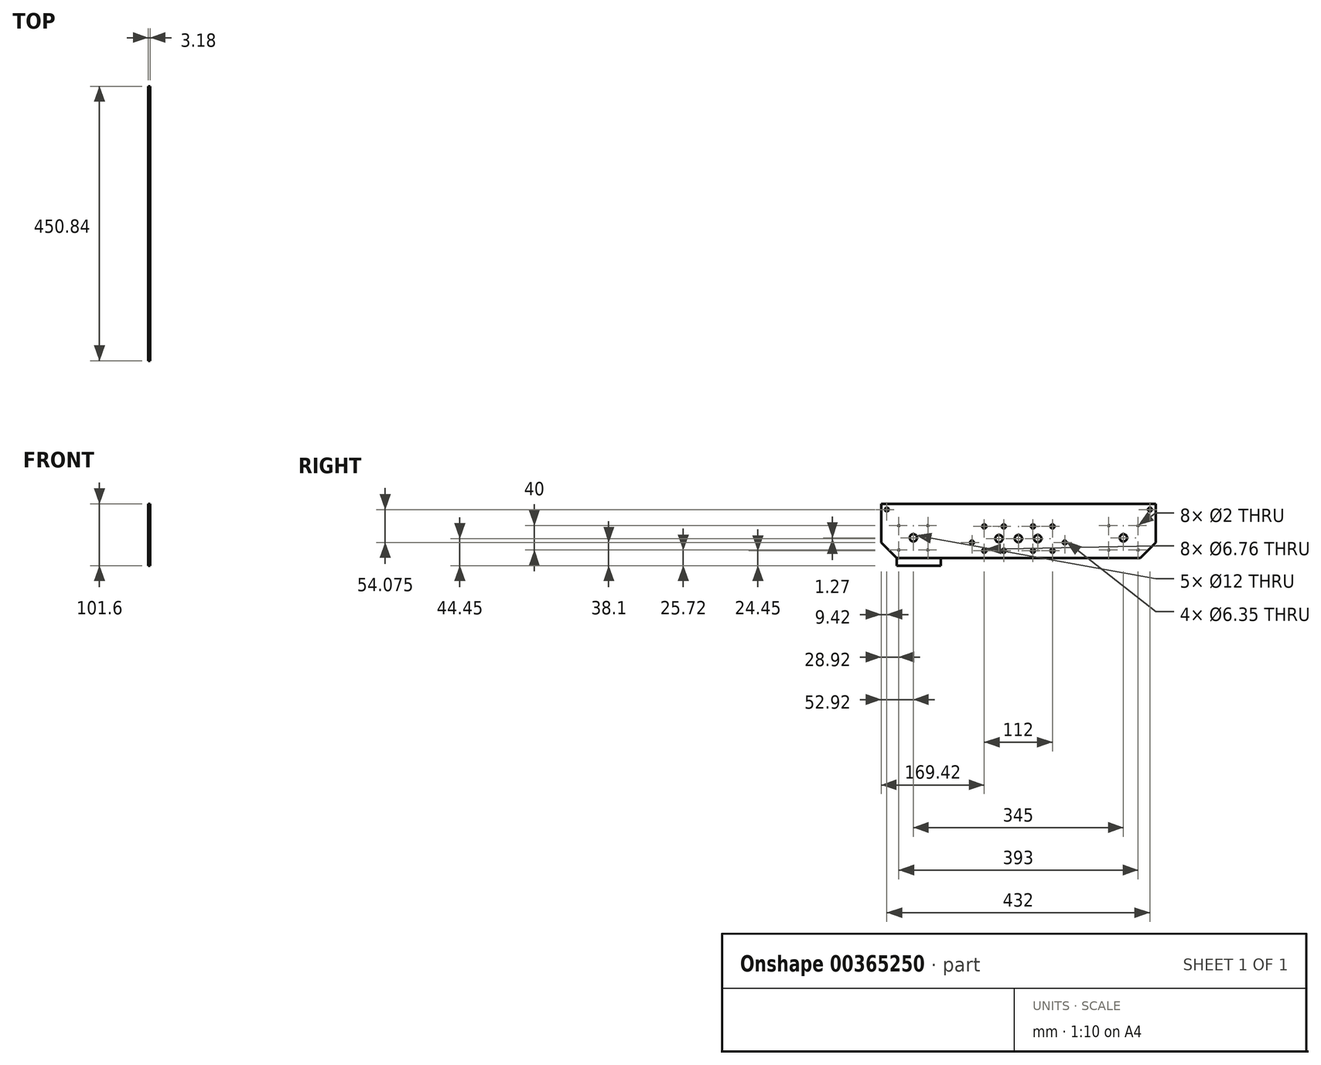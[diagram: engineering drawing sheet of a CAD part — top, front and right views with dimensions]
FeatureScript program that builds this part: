
annotation { "Feature Type Name" : "Feature", "Feature Type Description" : "" }
export const myFeature = defineFeature(function(context is Context, id is Id, definition is map)
    precondition{}
    {
        {
            var Q0;
            Q0=qCreatedBy(makeId("Right.planeOp"),FACE);
            cPlane(context, id + "F0", {"entities" : qUnion([Q0]), "cplaneType" : CPlaneType.OFFSET, "offset" : 142.88 * mm, "width" : 152.4 * mm, "height" : 152.4 * mm});
        }
        {
            var Q0;
            Q0=qCreatedBy(id+"F0.planeOp",FACE);
            var sketch = newSketch(context, id + "F1", { "sketchPlane" : qUnion([Q0])});
            skLineSegment(sketch, "E0.bottom", {"start": v(225.42, 44.45) * mm, "end": v(-225.43, 44.45) * mm});
            skLineSegment(sketch, "E0.top", {"start": v(200.02, -44.45) * mm, "end": v(-200.02, -44.45) * mm});
            skLineSegment(sketch, "E0.left", {"start": v(225.42, 44.45) * mm, "end": v(225.42, -19.05) * mm});
            skLineSegment(sketch, "E0.right", {"start": v(-225.43, 44.45) * mm, "end": v(-225.43, -19.05) * mm});
            skPoint(sketch, "E0.middle", {"position": v(0, 0) * mm});
            skLineSegment(sketch, "E1", {"start": v(-225.42, -19.05) * mm, "end": v(-200.02, -44.45) * mm});
            skLineSegment(sketch, "E2.MirrorCS", {"start": v(225.42, -19.05) * mm, "end": v(200.02, -44.45) * mm});
            skPoint(sketch, "E3.orphan", {"position": v(-225.42, -44.45) * mm});
            skLineSegment(sketch, "E4", {"start": v(-225.42, -19.05) * mm, "end": v(-225.42, -44.45) * mm, "construction": true});
            skLineSegment(sketch, "E5", {"start": v(-200.02, -44.45) * mm, "end": v(-225.42, -44.45) * mm, "construction": true});
            skPoint(sketch, "E6.orphan", {"position": v(225.43, -44.45) * mm});
            skSolve(sketch);
        }
        {
            var Q0;
            Q0=makeQuery(id+"F1.imprint","IMPRINT",FACE,{"disambiguationData":[TD([[makeQuery(id+"F1.imprint","IMPRINT",EDGE,{"derivedFrom":sQuery(id+"F1.wireOp",EDGE,"E0.bottom")}),1.0]])]});
            extrude(context, id + "F2", {"entities" : qUnion([Q0]), "depth" : 3.17 * mm, "offsetDistance" : 25.4 * mm});
        }
        {
            var Q0;
            Q0=makeQuery(id+"F2.opExtrude","CAP_FACE",FACE,{"disambiguationData":[OSD([sQuery(id+"F1.wireOp",EDGE,"E0.bottom"),sQuery(id+"F1.wireOp",EDGE,"E0.top"),sQuery(id+"F1.wireOp",EDGE,"E0.left"),sQuery(id+"F1.wireOp",EDGE,"E0.right"),sQuery(id+"F1.wireOp",EDGE,"E1"),sQuery(id+"F1.wireOp",EDGE,"E2.MirrorCS")])],"isStart":false});
            var sketch = newSketch(context, id + "F3", { "sketchPlane" : qUnion([Q0])});
            skCircle(sketch, "E7", {"center": v(0, -12.7) * mm, "radius": 6 * mm});
            skCircle(sketch, "E8", {"center": v(31.83, -12.7) * mm, "radius": 6 * mm});
            skCircle(sketch, "E9.MirrorC", {"center": v(-31.83, -12.7) * mm, "radius": 6 * mm});
            skCircle(sketch, "E10", {"center": v(172.5, -11.43) * mm, "radius": 6 * mm});
            skCircle(sketch, "E11", {"center": v(140.67, -11.43) * mm, "radius": 6 * mm, "construction": true});
            skCircle(sketch, "E12", {"center": v(108.85, -11.43) * mm, "radius": 6 * mm, "construction": true});
            skLineSegment(sketch, "E13", {"start": v(0, -12.7) * mm, "end": v(31.83, -12.7) * mm, "construction": true});
            skLineSegment(sketch, "E14", {"start": v(108.85, -11.43) * mm, "end": v(140.67, -11.43) * mm, "construction": true});
            skLineSegment(sketch, "E15", {"start": v(140.67, -11.43) * mm, "end": v(172.5, -11.43) * mm, "construction": true});
            skLineSegment(sketch, "E16.MirrorCS", {"start": v(-140.67, -11.43) * mm, "end": v(-172.5, -11.43) * mm, "construction": true});
            skCircle(sketch, "E17.MirrorC", {"center": v(-108.85, -11.43) * mm, "radius": 6 * mm, "construction": true});
            skLineSegment(sketch, "E18.MirrorCS", {"start": v(-108.85, -11.43) * mm, "end": v(-140.67, -11.43) * mm, "construction": true});
            skCircle(sketch, "E19.MirrorC", {"center": v(-140.67, -11.43) * mm, "radius": 6 * mm, "construction": true});
            skCircle(sketch, "E20.MirrorC", {"center": v(-172.5, -11.43) * mm, "radius": 6 * mm});
            skCircle(sketch, "E21", {"center": v(24, 7.3) * mm, "radius": 3.38 * mm});
            skCircle(sketch, "E22.MirrorC", {"center": v(24, -32.7) * mm, "radius": 3.38 * mm});
            skCircle(sketch, "E23.MirrorC", {"center": v(-24, 7.3) * mm, "radius": 3.38 * mm});
            skCircle(sketch, "E24.MirrorC", {"center": v(-24, -32.7) * mm, "radius": 3.38 * mm});
            skCircle(sketch, "E25", {"center": v(-56, 7.3) * mm, "radius": 3.38 * mm});
            skCircle(sketch, "E26.MirrorC", {"center": v(-56, -32.7) * mm, "radius": 3.38 * mm});
            skCircle(sketch, "E27.MirrorC", {"center": v(56, 7.3) * mm, "radius": 3.38 * mm});
            skCircle(sketch, "E28.MirrorC", {"center": v(56, -32.7) * mm, "radius": 3.38 * mm});
            skCircle(sketch, "E29", {"center": v(-148.5, 8.57) * mm, "radius": 1 * mm});
            skLineSegment(sketch, "E30", {"start": v(-172.5, -9.99) * mm, "end": v(-172.5, -13.98) * mm, "construction": true});
            skCircle(sketch, "E31.MirrorC", {"center": v(-196.5, 8.57) * mm, "radius": 1 * mm});
            skCircle(sketch, "E32.MirrorC", {"center": v(-148.5, -31.43) * mm, "radius": 1 * mm});
            skCircle(sketch, "E33.MirrorC", {"center": v(-196.5, -31.43) * mm, "radius": 1 * mm});
            skCircle(sketch, "E34.MirrorC", {"center": v(196.5, 8.57) * mm, "radius": 1 * mm});
            skCircle(sketch, "E35.MirrorC", {"center": v(148.5, 8.57) * mm, "radius": 1 * mm});
            skCircle(sketch, "E36.MirrorC", {"center": v(196.5, -31.43) * mm, "radius": 1 * mm});
            skCircle(sketch, "E37.MirrorC", {"center": v(148.5, -31.43) * mm, "radius": 1 * mm});
            skSolve(sketch);
        }
        {
            var Q0;
            Q0=makeQuery(id+"F2.opExtrude","CAP_FACE",FACE,{"disambiguationData":[OSD([sQuery(id+"F1.wireOp",EDGE,"E0.bottom"),sQuery(id+"F1.wireOp",EDGE,"E0.top"),sQuery(id+"F1.wireOp",EDGE,"E0.left"),sQuery(id+"F1.wireOp",EDGE,"E0.right"),sQuery(id+"F1.wireOp",EDGE,"E1"),sQuery(id+"F1.wireOp",EDGE,"E2.MirrorCS")])],"isStart":false});
            var sketch = newSketch(context, id + "F4", { "sketchPlane" : qUnion([Q0])});
            skPoint(sketch, "E38.0", {"position": v(0, -12.7) * mm});
            skPoint(sketch, "E39.0", {"position": v(172.5, -11.43) * mm});
            skPoint(sketch, "E39.1", {"position": v(-172.5, -11.43) * mm});
            skCircle(sketch, "E40", {"center": v(-172.5, -11.43) * mm, "radius": 50.8 * mm});
            skCircle(sketch, "E41", {"center": v(0, -12.7) * mm, "radius": 50.8 * mm});
            skCircle(sketch, "E42", {"center": v(172.5, -11.43) * mm, "radius": 50.8 * mm});
            skCircle(sketch, "E43", {"center": v(-172.5, -11.43) * mm, "radius": 19.1 * mm});
            skCircle(sketch, "E44", {"center": v(0, -12.7) * mm, "radius": 19.1 * mm});
            skCircle(sketch, "E45", {"center": v(172.5, -11.43) * mm, "radius": 19.1 * mm});
            skLineSegment(sketch, "E46", {"start": v(-172.5, 7.67) * mm, "end": v(0, 6.4) * mm});
            skLineSegment(sketch, "E47", {"start": v(-172.5, -30.53) * mm, "end": v(0, -31.8) * mm});
            skLineSegment(sketch, "E48", {"start": v(0, 6.4) * mm, "end": v(172.5, 7.67) * mm});
            skLineSegment(sketch, "E49", {"start": v(0, -31.8) * mm, "end": v(172.5, -30.53) * mm});
            skSolve(sketch);
        }
        {
            var Q0;
            Q0=makeQuery(id+"F2.opExtrude","CAP_FACE",FACE,{"disambiguationData":[OSD([sQuery(id+"F1.wireOp",EDGE,"E0.bottom"),sQuery(id+"F1.wireOp",EDGE,"E0.top"),sQuery(id+"F1.wireOp",EDGE,"E0.left"),sQuery(id+"F1.wireOp",EDGE,"E0.right"),sQuery(id+"F1.wireOp",EDGE,"E1"),sQuery(id+"F1.wireOp",EDGE,"E2.MirrorCS")])],"isStart":false});
            var sketch = newSketch(context, id + "F5", { "sketchPlane" : qUnion([Q0])});
            skCircle(sketch, "E50", {"center": v(-216, 35.02) * mm, "radius": 3.18 * mm});
            skCircle(sketch, "E51", {"center": v(-76.2, -19.05) * mm, "radius": 3.18 * mm});
            skCircle(sketch, "E52", {"center": v(-216, 35.02) * mm, "radius": 6.35 * mm, "construction": true});
            skCircle(sketch, "E53", {"center": v(-76.2, -19.05) * mm, "radius": 6.35 * mm, "construction": true});
            skCircle(sketch, "E54.MirrorC", {"center": v(216, 35.02) * mm, "radius": 3.18 * mm});
            skCircle(sketch, "E55.MirrorC", {"center": v(76.2, -19.05) * mm, "radius": 3.18 * mm});
            skCircle(sketch, "E56.MirrorC", {"center": v(216, 35.02) * mm, "radius": 6.35 * mm, "construction": true});
            skCircle(sketch, "E57.MirrorC", {"center": v(76.2, -19.05) * mm, "radius": 6.35 * mm, "construction": true});
            skPoint(sketch, "E58.0", {"position": v(0, -12.7) * mm});
            skSolve(sketch);
        }
        {
            var Q0;
            Q0 = qSketchRegion(id + "F3", true);
            var Q1;
            Q1 = qSketchRegion(id + "F5", true);
            var Q2;
            Q2=makeQuery(id+"F2.opExtrude","CAP_FACE",FACE,{"disambiguationData":[OSD([sQuery(id+"F1.wireOp",EDGE,"E0.bottom"),sQuery(id+"F1.wireOp",EDGE,"E0.top"),sQuery(id+"F1.wireOp",EDGE,"E0.left"),sQuery(id+"F1.wireOp",EDGE,"E0.right"),sQuery(id+"F1.wireOp",EDGE,"E1"),sQuery(id+"F1.wireOp",EDGE,"E2.MirrorCS")])],"isStart":true});
            extrude(context, id + "F6", {"entities" : qUnion([Q0, Q1]), "operationType" : NewBodyOperationType.REMOVE, "endBound" : BoundingType.UP_TO_SURFACE, "oppositeDirection" : true, "depth" : 25 * mm, "endBoundEntityFace" : qUnion([Q2]), "offsetDistance" : 25 * mm});
        }
        {
            var Q0;
            Q0=makeQuery(id+"F5.imprint","IMPRINT",FACE,{"disambiguationData":[TD([[makeQuery(id+"F5.imprint","IMPRINT",EDGE,{"derivedFrom":sQuery(id+"F5.wireOp",EDGE,"E50")}),-1.0]])]});
            var sketch = newSketch(context, id + "F7", { "sketchPlane" : qUnion([Q0])});
            skPoint(sketch, "E59.0", {"position": v(-200.02, -44.45) * mm});
            skLineSegment(sketch, "E60.bottom", {"start": v(-200.02, -44.45) * mm, "end": v(-127.43, -44.45) * mm});
            skLineSegment(sketch, "E60.top", {"start": v(-200.02, -57.15) * mm, "end": v(-127.43, -57.15) * mm});
            skLineSegment(sketch, "E60.left", {"start": v(-200.02, -44.45) * mm, "end": v(-200.02, -57.15) * mm});
            skLineSegment(sketch, "E60.right", {"start": v(-127.43, -44.45) * mm, "end": v(-127.43, -57.15) * mm});
            skSolve(sketch);
        }
        {
            var Q0;
            Q0 = qSketchRegion(id + "F7", true);
            extrude(context, id + "F8", {"entities" : qUnion([Q0]), "oppositeDirection" : true, "depth" : 3.17 * mm, "offsetDistance" : 25.4 * mm});
        }
    });
